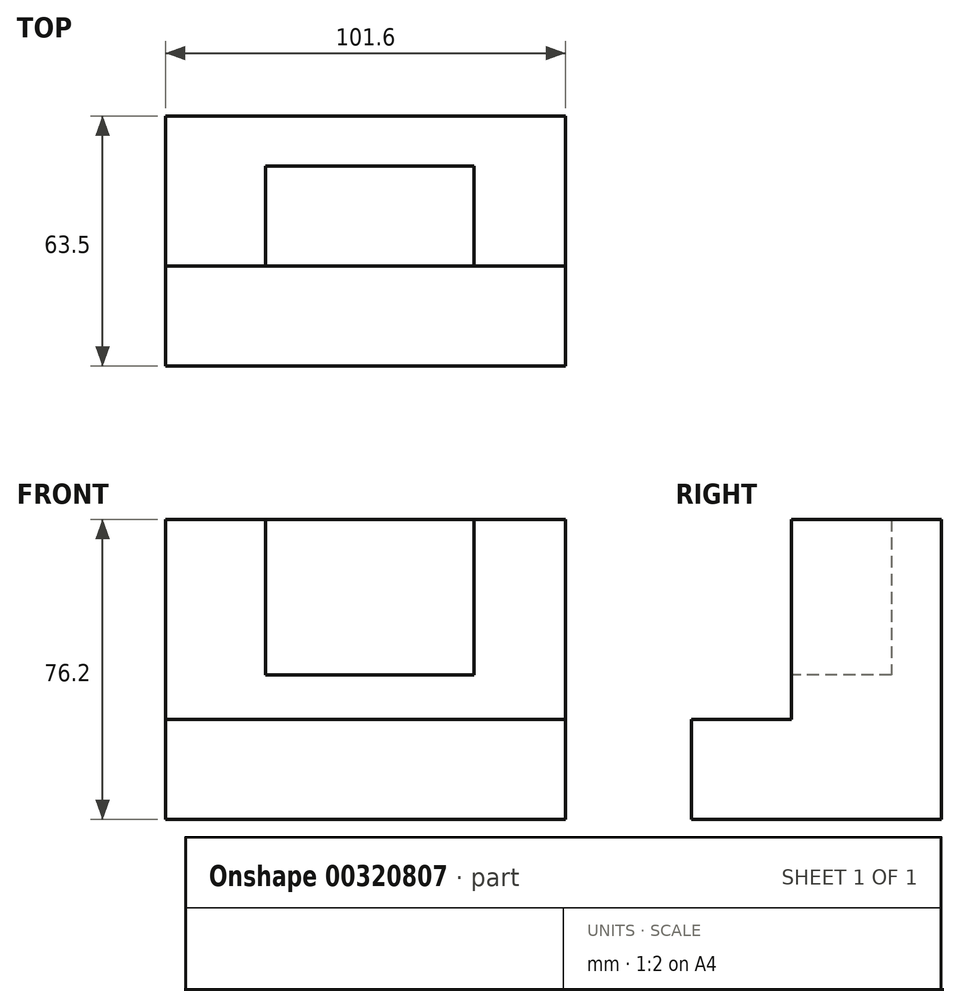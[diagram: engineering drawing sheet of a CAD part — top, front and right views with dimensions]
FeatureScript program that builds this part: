
annotation { "Feature Type Name" : "Feature", "Feature Type Description" : "" }
export const myFeature = defineFeature(function(context is Context, id is Id, definition is map)
    precondition{}
    {
        {
            var Q0;
            Q0=qCreatedBy(makeId("Right.planeOp"),FACE);
            var sketch = newSketch(context, id + "F0", { "sketchPlane" : qUnion([Q0])});
            skLineSegment(sketch, "E0", {"start": v(-48.69, -21.06) * mm, "end": v(14.81, -21.06) * mm});
            skLineSegment(sketch, "E1", {"start": v(14.81, -21.06) * mm, "end": v(14.81, 55.14) * mm});
            skLineSegment(sketch, "E2", {"start": v(14.81, 55.14) * mm, "end": v(-23.29, 55.14) * mm});
            skLineSegment(sketch, "E3", {"start": v(-23.29, 55.14) * mm, "end": v(-23.29, 4.34) * mm});
            skLineSegment(sketch, "E4", {"start": v(-23.29, 4.34) * mm, "end": v(-48.69, 4.34) * mm});
            skLineSegment(sketch, "E5", {"start": v(-48.69, 4.34) * mm, "end": v(-48.69, -21.06) * mm});
            skSolve(sketch);
        }
        {
            var Q0;
            Q0 = qSketchRegion(id + "F0", true);
            extrude(context, id + "F1", {"entities" : qUnion([Q0]), "depth" : 101.6 * mm});
        }
        {
            var Q0;
            Q0=makeQuery(id+"F1.opExtrude","SWEPT_FACE",FACE,{"disambiguationData":[OSD([sQuery(id+"F0.wireOp",EDGE,"E3")])]});
            var sketch = newSketch(context, id + "F2", { "sketchPlane" : qUnion([Q0])});
            skLineSegment(sketch, "E6", {"start": v(25.4, 55.14) * mm, "end": v(25.4, 15.63) * mm});
            skLineSegment(sketch, "E7", {"start": v(78.32, 15.63) * mm, "end": v(78.32, 55.14) * mm});
            skLineSegment(sketch, "E8", {"start": v(78.32, 55.14) * mm, "end": v(25.4, 55.14) * mm});
            skLineSegment(sketch, "E9", {"start": v(78.32, 15.63) * mm, "end": v(25.4, 15.63) * mm});
            skSolve(sketch);
        }
        {
            var Q0;
            Q0 = qSketchRegion(id + "F2", true);
            extrude(context, id + "F3", {"entities" : qUnion([Q0]), "operationType" : NewBodyOperationType.REMOVE, "oppositeDirection" : true, "depth" : 25.4 * mm});
        }
    });
